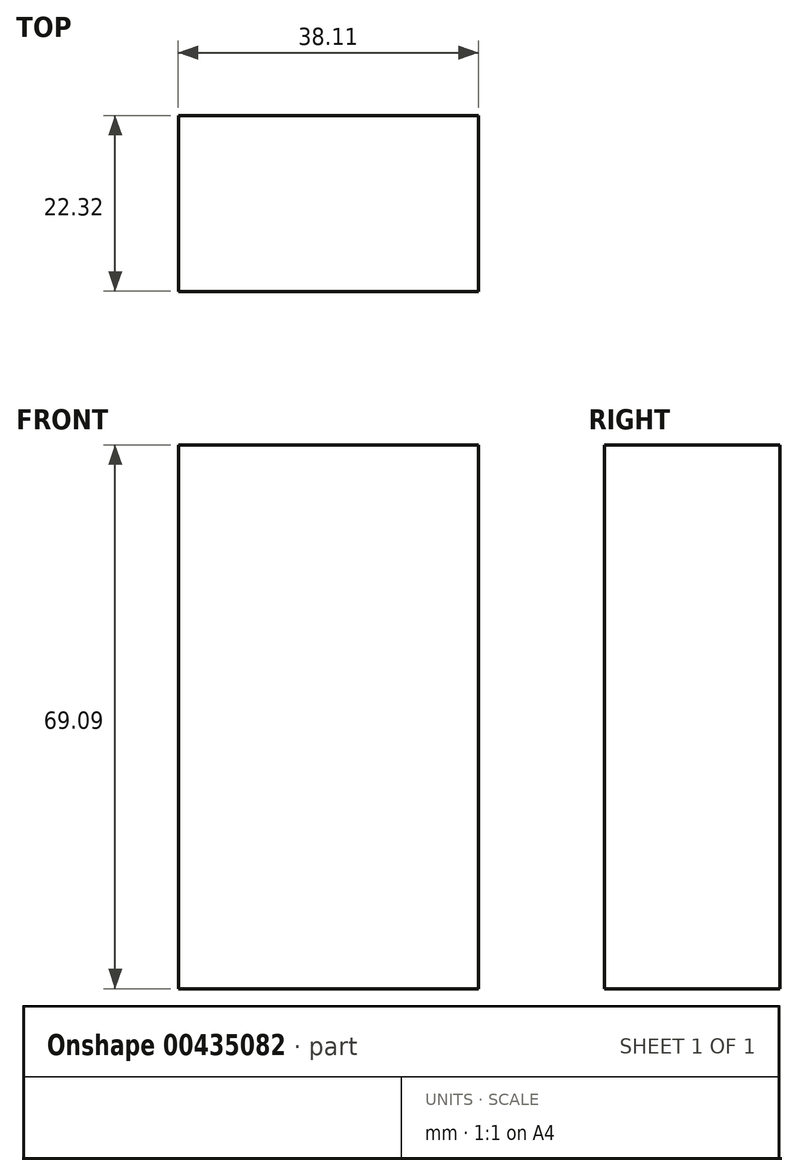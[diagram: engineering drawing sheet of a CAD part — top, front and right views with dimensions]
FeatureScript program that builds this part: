
annotation { "Feature Type Name" : "Feature", "Feature Type Description" : "" }
export const myFeature = defineFeature(function(context is Context, id is Id, definition is map)
    precondition{}
    {
        {
            var Q0;
            Q0=qCreatedBy(makeId("Top.planeOp"),FACE);
            var sketch = newSketch(context, id + "F0", { "sketchPlane" : qUnion([Q0])});
            skLineSegment(sketch, "E0.bottom", {"start": v(-70.32, -46.33) * mm, "end": v(-32.2, -46.33) * mm});
            skLineSegment(sketch, "E0.top", {"start": v(-70.32, -68.65) * mm, "end": v(-32.2, -68.65) * mm});
            skLineSegment(sketch, "E0.left", {"start": v(-70.32, -46.33) * mm, "end": v(-70.32, -68.65) * mm});
            skLineSegment(sketch, "E0.right", {"start": v(-32.2, -46.33) * mm, "end": v(-32.2, -68.65) * mm});
            skSolve(sketch);
        }
        {
            var Q0;
            Q0=makeQuery(id+"F0.imprint","IMPRINT",FACE,{"disambiguationData":[TD([[makeQuery(id+"F0.imprint","IMPRINT",EDGE,{"derivedFrom":sQuery(id+"F0.wireOp",EDGE,"E0.bottom")}),-1.0]])]});
            extrude(context, id + "F1", {"entities" : qUnion([Q0]), "depth" : 69.1 * mm});
        }
    });
